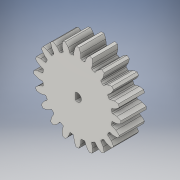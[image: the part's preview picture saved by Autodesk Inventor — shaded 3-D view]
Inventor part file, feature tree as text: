
AUTODESK INVENTOR PART (.ipt)
format: ipt  version: 2016 (Build 200138000, 138)  size: 446,976 bytes
history: native  units: in
note: dims shown in document units (in); Inventor stores cm internally (conversion verified against a paired STEP export)
features: sketch x4, extrude x2
ambient origin geometry x8: Origin, YZ Plane, XZ Plane, XY Plane, X Axis, Y Axis, Z Axis, Center Point
bodies: Solid1 (feature_tree)
feature tree (6):
  extrude  "Extrusion1"  Depth=0.5in
  extrude  "Extrusion2"  Depth=0.37in TaperAngle=0.0deg
  sketch  "Sketch4"
  sketch  "Sketch5"
  sketch  "Sketch2"  dims[d0=0.5in d1=0.0in d2=0.1575in]
  sketch  "Sketch3"  dims[d3=0.04in d4=0.37in d5=0.0in]
